# Revit family: 210_CAD O Integral EX 60 VLEXG
name_source: partatom
category: Mechanical Equipment
units: mm (PartAtom-declared; Revit-internal decimal feet)

## family parameters
Always vertical = Yes
Cut with Voids When Loaded = No
Part Type = Breaks Into
Room Calculation Point = No
Round Connector Dimension = Use Diameter
Shared = No
Work Plane-Based = No

## types (1)
- CAD O Integral EX 60 VLEXG
    AA1 = 986 mm  [stored 3.23491 ft]
    B = 700 mm
    BB1 = 658 mm
    BH1 = 390 mm  [stored 1.27953 ft]
    BH2 = 2 mm  [stored 0.00656168 ft]
    BH2__ve = -2 mm  [stored -0.00656168 ft]
    BH3 = 590 mm  [stored 1.9357 ft]
    BH4 = 195 mm  [stored 0.639764 ft]
    BH5 = 875 mm  [stored 2.87073 ft]
    CAT0 = Yes
    H = 510 mm
    HH1 = 1553 mm  [stored 5.09514 ft]
    MM1 = 490 mm  [stored 1.60761 ft]
    MM2 = 1170 mm  [stored 3.83858 ft]
    SPNN = 2232 mm  [stored 7.32283 ft]
    SPR = 106 mm  [stored 0.347769 ft]
    SPS = 54 mm  [stored 0.177165 ft]
    SS1 = 750 mm  [stored 2.46063 ft]
    SS2 = 1116 mm  [stored 3.66142 ft]
    W = 500 mm  [stored 1.64042 ft]
    magiPartTypeId = 210
    magiProductCode = CAD O Integral EX 60 VLEXG
    magiProductFamilyId = CAD O Integral EX 60 VLEXG
    magiProductId = CAD O Integral EX 60 VLEXG

note: [stored X ft] marks values corroborated as IEEE doubles in the binary element streams (Revit-internal decimal feet)

## geometry (parser evidence)
native form markers: Sweep x3
no freeform markers — native parametric forms only
